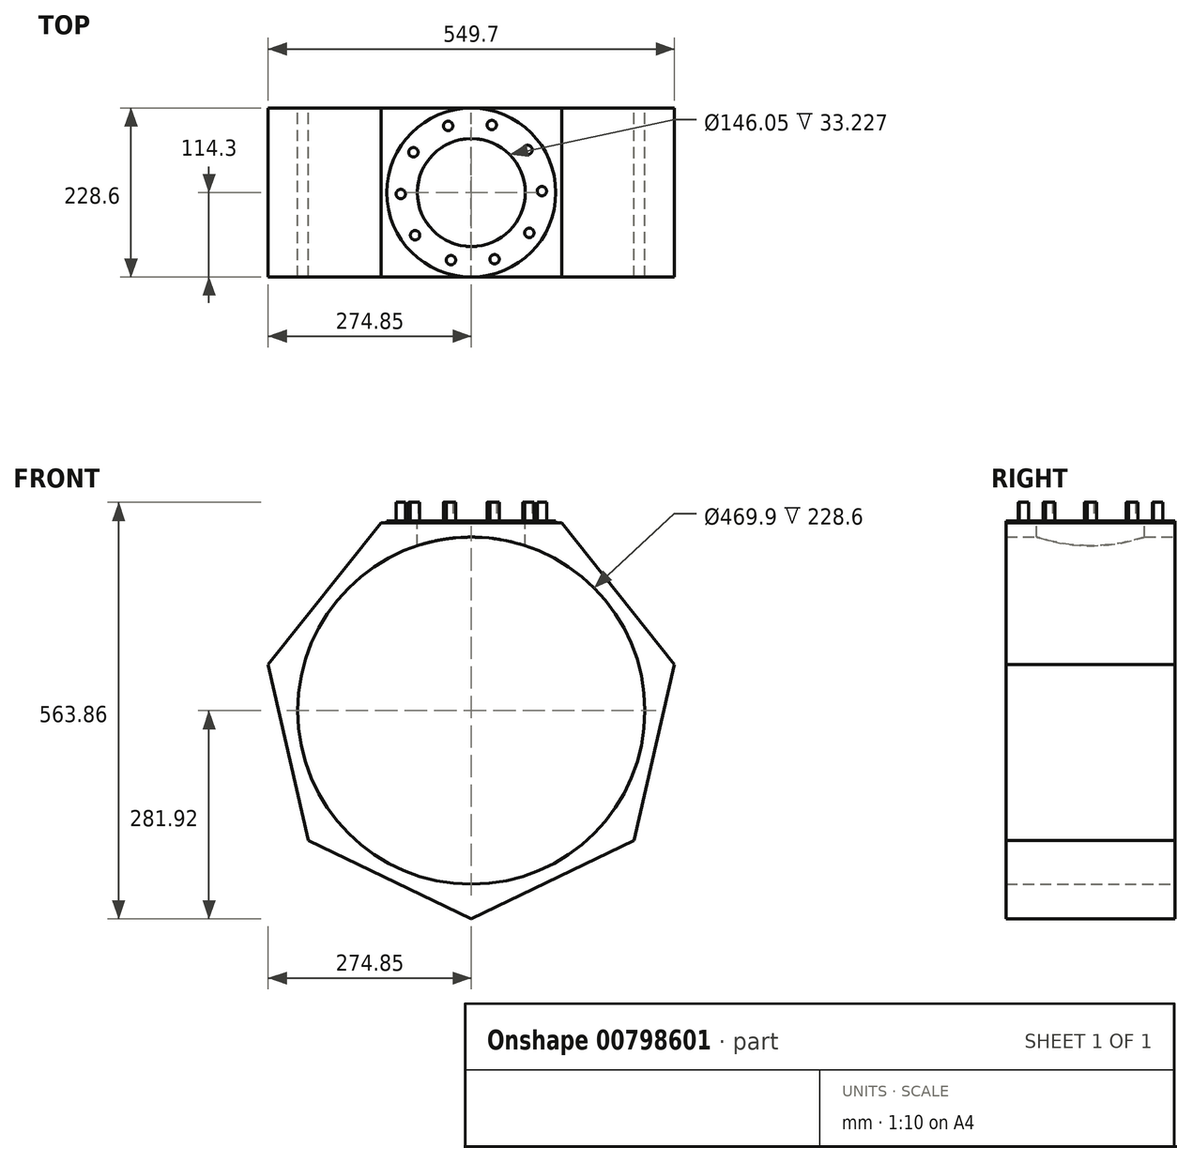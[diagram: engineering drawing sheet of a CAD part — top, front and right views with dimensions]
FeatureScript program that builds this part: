
annotation { "Feature Type Name" : "Feature", "Feature Type Description" : "" }
export const myFeature = defineFeature(function(context is Context, id is Id, definition is map)
    precondition{}
    {
        {
            var Q0;
            Q0=qCreatedBy(makeId("Front.planeOp"),FACE);
            var sketch = newSketch(context, id + "F0", { "sketchPlane" : qUnion([Q0])});
            skCircle(sketch, "E0.cCircle", {"center": v(0, 0) * mm, "radius": 241.3 * mm, "construction": true});
            skLineSegment(sketch, "E0.0", {"start": v(-116.2, 241.3) * mm, "end": v(116.2, 241.3) * mm});
            skLineSegment(sketch, "E0.1", {"start": v(116.2, 241.3) * mm, "end": v(261.1, 59.6) * mm});
            skLineSegment(sketch, "E0.2", {"start": v(261.1, 59.6) * mm, "end": v(209.4, -166.98) * mm});
            skLineSegment(sketch, "E0.3", {"start": v(209.4, -166.98) * mm, "end": v(0, -267.82) * mm});
            skLineSegment(sketch, "E0.4", {"start": v(0, -267.82) * mm, "end": v(-209.4, -166.98) * mm});
            skLineSegment(sketch, "E0.5", {"start": v(-209.4, -166.98) * mm, "end": v(-261.1, 59.6) * mm});
            skLineSegment(sketch, "E0.6", {"start": v(-261.1, 59.6) * mm, "end": v(-116.2, 241.3) * mm});
            skPoint(sketch, "E0.0.midPoint", {"position": v(0, 241.3) * mm});
            skLineSegment(sketch, "E1.0", {"start": v(-274.85, 62.73) * mm, "end": v(-122.32, 254) * mm});
            skLineSegment(sketch, "E1.1", {"start": v(-220.41, -175.77) * mm, "end": v(-274.85, 62.73) * mm});
            skLineSegment(sketch, "E1.2", {"start": v(122.32, 254) * mm, "end": v(274.85, 62.73) * mm});
            skLineSegment(sketch, "E1.3", {"start": v(274.85, 62.73) * mm, "end": v(220.41, -175.77) * mm});
            skLineSegment(sketch, "E1.4", {"start": v(220.41, -175.77) * mm, "end": v(0, -281.92) * mm});
            skLineSegment(sketch, "E1.5", {"start": v(-122.32, 254) * mm, "end": v(122.32, 254) * mm});
            skLineSegment(sketch, "E1.6", {"start": v(0, -281.92) * mm, "end": v(-220.41, -175.77) * mm});
            skSolve(sketch);
        }
        {
            var Q0;
            Q0=makeQuery(id+"F0.imprint","IMPRINT",FACE,{"disambiguationData":[TD([[makeQuery(id+"F0.imprint","IMPRINT",EDGE,{"derivedFrom":sQuery(id+"F0.wireOp",EDGE,"E0.0")}),1.0]])]});
            extrude(context, id + "F1", {"entities" : qUnion([Q0]), "endBound" : BoundingType.SYMMETRIC, "depth" : 228.6 * mm, "offsetDistance" : 25.4 * mm});
        }
        {
            var Q0;
            Q0=qCreatedBy(makeId("Front.planeOp"),FACE);
            var sketch = newSketch(context, id + "F2", { "sketchPlane" : qUnion([Q0])});
            skCircle(sketch, "E2", {"center": v(0, 0) * mm, "radius": 234.95 * mm});
            skLineSegment(sketch, "E3.0", {"start": v(-261.1, 59.6) * mm, "end": v(-116.2, 241.3) * mm});
            skLineSegment(sketch, "E4.0", {"start": v(-116.2, 241.3) * mm, "end": v(116.2, 241.3) * mm});
            skLineSegment(sketch, "E5.0", {"start": v(116.2, 241.3) * mm, "end": v(261.1, 59.6) * mm});
            skLineSegment(sketch, "E6.0", {"start": v(261.1, 59.6) * mm, "end": v(209.4, -166.98) * mm});
            skLineSegment(sketch, "E7.0", {"start": v(209.4, -166.98) * mm, "end": v(0, -267.82) * mm});
            skLineSegment(sketch, "E8.0", {"start": v(0, -267.82) * mm, "end": v(-209.4, -166.98) * mm});
            skLineSegment(sketch, "E9.0", {"start": v(-209.4, -166.98) * mm, "end": v(-261.1, 59.6) * mm});
            skSolve(sketch);
        }
        {
            var Q0;
            Q0=makeQuery(id+"F2.imprint","IMPRINT",FACE,{"disambiguationData":[TD([[makeQuery(id+"F2.imprint","IMPRINT",EDGE,{"derivedFrom":sQuery(id+"F2.wireOp",EDGE,"E2")}),-1.0]])]});
            extrude(context, id + "F3", {"entities" : qUnion([Q0]), "operationType" : NewBodyOperationType.ADD, "endBound" : BoundingType.SYMMETRIC, "depth" : 228.6 * mm, "offsetDistance" : 25.4 * mm});
        }
        {
            var Q0;
            Q0=makeQuery(id+"F1.opExtrude","SWEPT_FACE",FACE,{"disambiguationData":[OSD([sQuery(id+"F0.wireOp",EDGE,"E1.5")])]});
            var sketch = newSketch(context, id + "F4", { "sketchPlane" : qUnion([Q0])});
            skCircle(sketch, "E10", {"center": v(0, 0) * mm, "radius": 73.03 * mm});
            skSolve(sketch);
        }
        {
            var Q0;
            Q0=makeQuery(id+"F4.imprint","IMPRINT",FACE,{"disambiguationData":[TD([[makeQuery(id+"F4.imprint","IMPRINT",EDGE,{"derivedFrom":sQuery(id+"F4.wireOp",EDGE,"E10")}),1.0]])]});
            extrude(context, id + "F5", {"entities" : qUnion([Q0]), "operationType" : NewBodyOperationType.REMOVE, "oppositeDirection" : true, "depth" : 76.2 * mm, "offsetDistance" : 25.4 * mm});
        }
        {
            var Q0;
            Q0=makeQuery(id+"F1.opExtrude","SWEPT_FACE",FACE,{"disambiguationData":[OSD([sQuery(id+"F0.wireOp",EDGE,"E1.5")])]});
            var sketch = newSketch(context, id + "F6", { "sketchPlane" : qUnion([Q0])});
            skCircle(sketch, "E11.cCircle", {"center": v(0, 0) * mm, "radius": 85.1 * mm, "construction": true});
            skLineSegment(sketch, "E11.0", {"start": v(27.65, -85.1) * mm, "end": v(-27.65, -85.1) * mm});
            skLineSegment(sketch, "E11.1", {"start": v(-27.65, -85.1) * mm, "end": v(-72.38, -52.59) * mm});
            skLineSegment(sketch, "E11.2", {"start": v(-72.38, -52.59) * mm, "end": v(-89.47, 0) * mm});
            skLineSegment(sketch, "E11.3", {"start": v(-89.47, 0) * mm, "end": v(-72.38, 52.59) * mm});
            skLineSegment(sketch, "E11.4", {"start": v(-72.38, 52.59) * mm, "end": v(-27.65, 85.1) * mm});
            skLineSegment(sketch, "E11.5", {"start": v(-27.65, 85.09) * mm, "end": v(27.65, 85.1) * mm});
            skLineSegment(sketch, "E11.6", {"start": v(27.65, 85.1) * mm, "end": v(72.38, 52.59) * mm});
            skLineSegment(sketch, "E11.7", {"start": v(72.38, 52.59) * mm, "end": v(89.47, 0) * mm});
            skLineSegment(sketch, "E11.8", {"start": v(89.47, 0) * mm, "end": v(72.38, -52.59) * mm});
            skLineSegment(sketch, "E11.9", {"start": v(72.38, -52.59) * mm, "end": v(27.65, -85.09) * mm});
            skPoint(sketch, "E11.0.midPoint", {"position": v(0, -85.1) * mm});
            skCircle(sketch, "E12", {"center": v(0, 0) * mm, "radius": 114.3 * mm});
            skCircle(sketch, "E13", {"center": v(0, 0) * mm, "radius": 73.03 * mm});
            skSolve(sketch);
        }
        {
            var Q0;
            Q0=makeQuery(id+"F6.imprint","IMPRINT",FACE,{"disambiguationData":[TD([[makeQuery(id+"F6.imprint","IMPRINT",EDGE,{"derivedFrom":sQuery(id+"F6.wireOp",EDGE,"E11.0")}),1.0]])]});
            var Q1;
            Q1=makeQuery(id+"F6.imprint","IMPRINT",FACE,{"disambiguationData":[TD([[makeQuery(id+"F6.imprint","IMPRINT",EDGE,{"derivedFrom":sQuery(id+"F6.wireOp",EDGE,"E11.0")}),-1.0]])]});
            extrude(context, id + "F7", {"entities" : qUnion([Q0, Q1]), "operationType" : NewBodyOperationType.ADD, "depth" : 2.54 * mm, "offsetDistance" : 25.4 * mm});
        }
        {
            var Q0;
            Q0=makeQuery(id+"F7.opExtrude","CAP_FACE",FACE,{"disambiguationData":[OSD([sQuery(id+"F6.wireOp",EDGE,"E12"),sQuery(id+"F6.wireOp",EDGE,"E13")])],"isStart":false});
            var sketch = newSketch(context, id + "F8", { "sketchPlane" : qUnion([Q0])});
            skCircle(sketch, "E14.cCircle", {"center": v(0, 0) * mm, "radius": 91.44 * mm, "construction": true});
            skPoint(sketch, "E14.0.midPoint", {"position": v(0, 91.44) * mm});
            skCircle(sketch, "E15", {"center": v(27.65, 91.44) * mm, "radius": 6.35 * mm});
            skCircle(sketch, "E16.1.0", {"center": v(-31.38, 90.23) * mm, "radius": 6.35 * mm});
            skCircle(sketch, "E16.2.0", {"center": v(-78.42, 54.55) * mm, "radius": 6.35 * mm});
            skCircle(sketch, "E16.3.0", {"center": v(-95.5, -1.96) * mm, "radius": 6.35 * mm});
            skCircle(sketch, "E16.4.0", {"center": v(-76.11, -57.73) * mm, "radius": 6.35 * mm});
            skCircle(sketch, "E16.5.0", {"center": v(-27.65, -91.44) * mm, "radius": 6.35 * mm});
            skCircle(sketch, "E16.6.0", {"center": v(31.38, -90.23) * mm, "radius": 6.35 * mm});
            skCircle(sketch, "E16.7.0", {"center": v(78.42, -54.55) * mm, "radius": 6.35 * mm});
            skCircle(sketch, "E16.8.0", {"center": v(95.5, 1.96) * mm, "radius": 6.35 * mm});
            skCircle(sketch, "E16.9.0", {"center": v(76.11, 57.73) * mm, "radius": 6.35 * mm});
            skPoint(sketch, "E17.orphan", {"position": v(-27.65, 91.44) * mm});
            skPoint(sketch, "E18.orphan", {"position": v(72.38, 52.59) * mm});
            skPoint(sketch, "E19.orphan", {"position": v(89.47, 0) * mm});
            skPoint(sketch, "E20.orphan", {"position": v(72.38, -52.59) * mm});
            skPoint(sketch, "E21.orphan", {"position": v(27.65, -85.1) * mm});
            skPoint(sketch, "E22.orphan", {"position": v(-27.65, -85.1) * mm});
            skPoint(sketch, "E23.orphan", {"position": v(-72.38, -52.59) * mm});
            skPoint(sketch, "E24.orphan", {"position": v(-89.47, 0) * mm});
            skPoint(sketch, "E25.orphan", {"position": v(-72.38, 52.59) * mm});
            skSolve(sketch);
        }
        {
            var Q0;
            Q0=makeQuery(id+"F8.imprint","IMPRINT",FACE,{"disambiguationData":[TD([[makeQuery(id+"F8.imprint","IMPRINT",EDGE,{"derivedFrom":sQuery(id+"F8.wireOp",EDGE,"E16.1.0")}),1.0]])]});
            var Q1;
            Q1=makeQuery(id+"F8.imprint","IMPRINT",FACE,{"disambiguationData":[TD([[makeQuery(id+"F8.imprint","IMPRINT",EDGE,{"derivedFrom":sQuery(id+"F8.wireOp",EDGE,"E16.2.0")}),1.0]])]});
            var Q2;
            Q2=makeQuery(id+"F8.imprint","IMPRINT",FACE,{"disambiguationData":[TD([[makeQuery(id+"F8.imprint","IMPRINT",EDGE,{"derivedFrom":sQuery(id+"F8.wireOp",EDGE,"E16.3.0")}),1.0]])]});
            var Q3;
            Q3=makeQuery(id+"F8.imprint","IMPRINT",FACE,{"disambiguationData":[TD([[makeQuery(id+"F8.imprint","IMPRINT",EDGE,{"derivedFrom":sQuery(id+"F8.wireOp",EDGE,"E16.4.0")}),1.0]])]});
            var Q4;
            Q4=makeQuery(id+"F8.imprint","IMPRINT",FACE,{"disambiguationData":[TD([[makeQuery(id+"F8.imprint","IMPRINT",EDGE,{"derivedFrom":sQuery(id+"F8.wireOp",EDGE,"E16.5.0")}),1.0]])]});
            var Q5;
            Q5=makeQuery(id+"F8.imprint","IMPRINT",FACE,{"disambiguationData":[TD([[makeQuery(id+"F8.imprint","IMPRINT",EDGE,{"derivedFrom":sQuery(id+"F8.wireOp",EDGE,"E16.6.0")}),1.0]])]});
            var Q6;
            Q6=makeQuery(id+"F8.imprint","IMPRINT",FACE,{"disambiguationData":[TD([[makeQuery(id+"F8.imprint","IMPRINT",EDGE,{"derivedFrom":sQuery(id+"F8.wireOp",EDGE,"E16.7.0")}),1.0]])]});
            var Q7;
            Q7=makeQuery(id+"F8.imprint","IMPRINT",FACE,{"disambiguationData":[TD([[makeQuery(id+"F8.imprint","IMPRINT",EDGE,{"derivedFrom":sQuery(id+"F8.wireOp",EDGE,"E16.8.0")}),1.0]])]});
            var Q8;
            Q8=makeQuery(id+"F8.imprint","IMPRINT",FACE,{"disambiguationData":[TD([[makeQuery(id+"F8.imprint","IMPRINT",EDGE,{"derivedFrom":sQuery(id+"F8.wireOp",EDGE,"E16.9.0")}),1.0]])]});
            var Q9;
            Q9=makeQuery(id+"F8.imprint","IMPRINT",FACE,{"disambiguationData":[TD([[makeQuery(id+"F8.imprint","IMPRINT",EDGE,{"derivedFrom":sQuery(id+"F8.wireOp",EDGE,"E15")}),1.0]])]});
            extrude(context, id + "F9", {"entities" : qUnion([Q0, Q1, Q2, Q3, Q4, Q5, Q6, Q7, Q8, Q9]), "operationType" : NewBodyOperationType.ADD, "depth" : 25.4 * mm, "offsetDistance" : 25.4 * mm});
        }
    });
